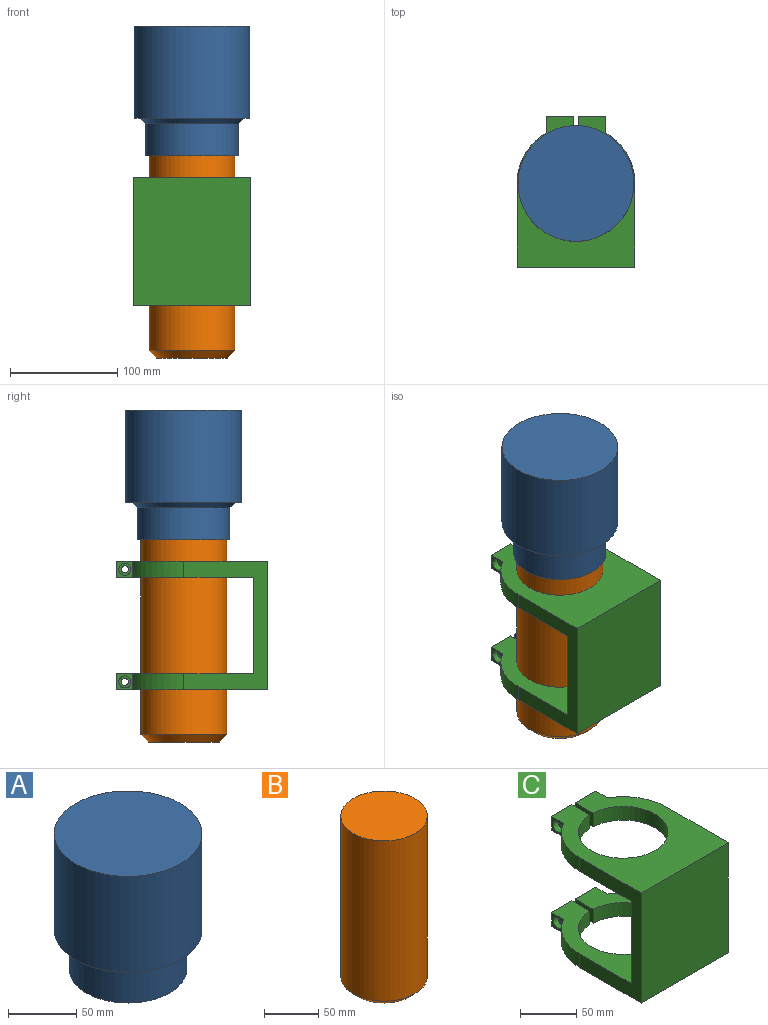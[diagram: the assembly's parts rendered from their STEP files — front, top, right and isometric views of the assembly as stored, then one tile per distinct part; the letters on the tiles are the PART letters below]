
ASSEMBLY  parts=3 mates=2
PART A: 6 faces, bbox 108x108x121 mm
  f0: cylinder r=43mm len=86mm, axis (0,0,-1), area 8105.3mm2, adj f1,f5
  f1: plane 86x86mm, normal (0,0,-1), area 5808.8mm2, adj f0
  f2: cylinder r=54mm len=108mm, axis (0,0,-1), area 29179.1mm2, adj f3,f4
  f3: plane 108x108mm, normal (0,0,1), area 9160.9mm2, adj f2
  f4: plane 108x108mm, normal (0,0,-1), area 1922.7mm2, adj f2,f5
  f5: cone r=48mm half-angle=45deg, axis (0,0,1), area 2021.5mm2, adj f0,f4
PART B: 4 faces, bbox 80x80x188.5 mm
  f0: cylinder r=40mm len=181.5mm, axis (0,0,-1), area 45615.9mm2, adj f1,f3
  f1: plane 80x80mm, normal (0,0,1), area 5026.5mm2, adj f0
  f2: plane 66x66mm, normal (0,0,-1), area 3421.2mm2, adj f3
  f3: cone r=40mm half-angle=45deg, axis (0,0,1), area 2270.3mm2, adj f0,f2
PART C: 34 faces, bbox 110x140.2x120 mm
  f0: cylinder r=55mm len=47.5mm, axis (0,0,-1), area 860mm2, adj f1,f10,f11,f12
  f1: plane 120x77.7mm, normal (-1,0,0), area 3474mm2, adj f0,f11,f12,f17,f18,f19,f28,f29
  f2: plane 120x77.7mm, normal (1,0,0), area 3474mm2, adj f3,f11,f12,f17,f18,f20,f28,f29
  f3: cylinder r=55mm len=47.5mm, axis (0,0,-1), area 860mm2, adj f2,f4,f11,f12
  f4: plane 15x15mm, normal (1,0,0), area 190.8mm2, adj f3,f5,f11,f12,f16
  f5: plane 25.73x15mm, normal (0,1,0), area 385.9mm2, adj f4,f6,f11,f12
  f6: plane 22.55x15mm, normal (-1,0,0), area 304mm2, adj f5,f7,f11,f12,f16
  f7: cylinder r=40mm len=80mm, axis (0,0,-1), area 3709.9mm2, adj f6,f8,f11,f12
  f8: plane 22.55x15mm, normal (1,0,0), area 304mm2, adj f7,f9,f11,f12,f13
  f9: plane 25.73x15mm, normal (0,1,0), area 385.9mm2, adj f8,f10,f11,f12
  f10: plane 15x15mm, normal (-1,0,0), area 125.6mm2, adj f0,f9,f11,f12,f15
  f11: plane 127.5x110mm, normal (0,0,1), area 7335.6mm2, adj f0,f1,f2,f3,f4,f5,f6,f7
  f12: plane 140.2x110mm, normal (0,0,-1), area 8732.6mm2, adj f0,f1,f2,f3,f4,f5,f6,f7
  f13: cylinder r=3.3mm len=19.73mm, axis (-1,0,0), area 409mm2, adj f8,f14
  f14: plane 11.25x11.25mm, normal (-1,0,0), area 65.2mm2, adj f13,f15
  f15: cylinder r=5.62mm len=11.25mm, axis (-1,0,0), area 212.1mm2, adj f10,f14
  f16: cylinder r=3.3mm len=25.73mm, axis (-1,0,0), area 533.4mm2, adj f4,f6
  f17: plane 110x90mm, normal (0,1,0), area 9900mm2, adj f1,f2,f11,f28
  f18: plane 120x110mm, normal (0,-1,0), area 13200mm2, adj f1,f2,f12,f29
  f19: cylinder r=55mm len=47.5mm, axis (0,0,1), area 860mm2, adj f1,f27,f28,f29
  f20: cylinder r=55mm len=47.5mm, axis (0,0,1), area 860mm2, adj f2,f21,f28,f29
  f21: plane 15x15mm, normal (1,0,0), area 190.8mm2, adj f20,f22,f28,f29,f33
  f22: plane 25.73x15mm, normal (0,1,0), area 385.9mm2, adj f21,f23,f28,f29
  f23: plane 22.55x15mm, normal (-1,0,0), area 304mm2, adj f22,f24,f28,f29,f33
  f24: cylinder r=40mm len=80mm, axis (0,0,1), area 3709.9mm2, adj f23,f25,f28,f29
  f25: plane 22.55x15mm, normal (1,0,0), area 304mm2, adj f24,f26,f28,f29,f30
  f26: plane 25.73x15mm, normal (0,1,0), area 385.9mm2, adj f25,f27,f28,f29
  f27: plane 15x15mm, normal (-1,0,0), area 125.6mm2, adj f19,f26,f28,f29,f32
  f28: plane 127.5x110mm, normal (0,0,-1), area 7335.6mm2, adj f1,f2,f17,f19,f20,f21,f22,f23
  f29: plane 140.2x110mm, normal (0,0,1), area 8732.6mm2, adj f1,f2,f18,f19,f20,f21,f22,f23
  f30: cylinder r=3.3mm len=19.73mm, axis (-1,0,0), area 409mm2, adj f25,f31
  f31: plane 11.25x11.25mm, normal (-1,0,0), area 65.2mm2, adj f30,f32
  f32: cylinder r=5.62mm len=11.25mm, axis (-1,0,0), area 212.1mm2, adj f27,f31
  f33: cylinder r=3.3mm len=25.73mm, axis (-1,0,0), area 533.4mm2, adj f21,f23
PLACE A t=(0,0,197.36)mm
PLACE B t=(0,0,197.36)mm
PLACE C t=(0,0,222.86)mm
MATE fastened B.f0 <-> A.f0  axis (0,0,1) through (0,0,362.86)mm
MATE fastened C.f7 <-> B.f0  axis (0,0,1) through (0,0,342.86)mm
